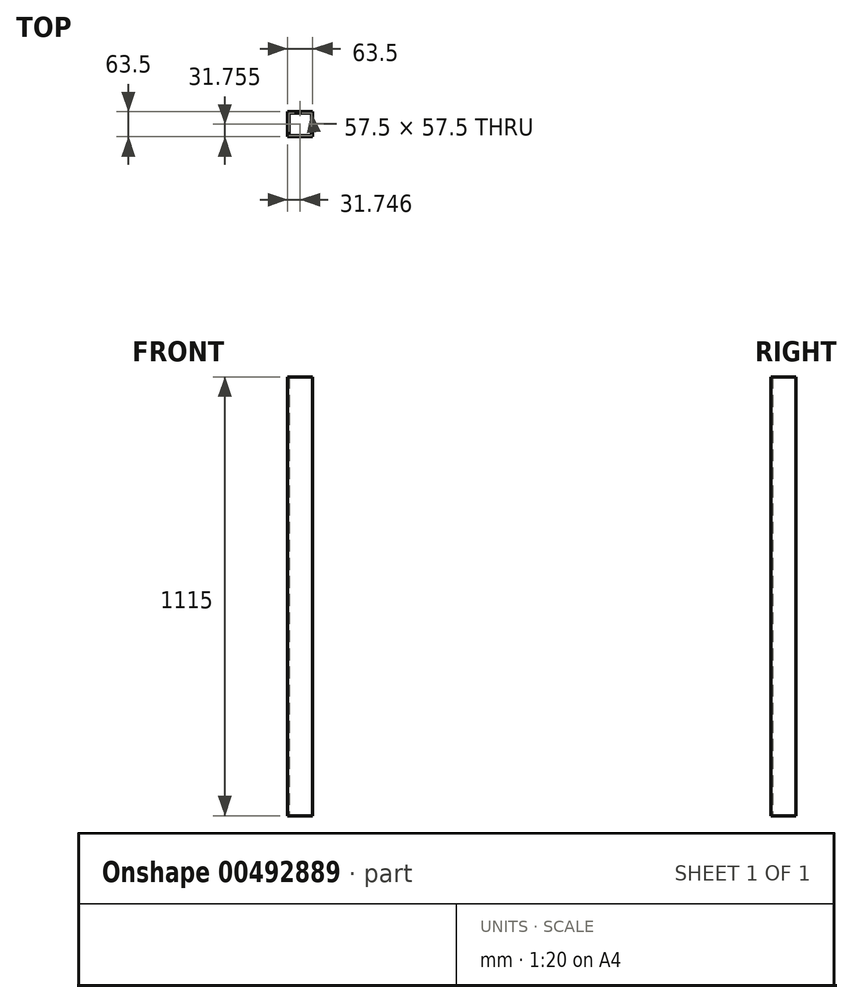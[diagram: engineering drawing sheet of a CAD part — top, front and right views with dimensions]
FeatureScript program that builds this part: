
annotation { "Feature Type Name" : "Feature", "Feature Type Description" : "" }
export const myFeature = defineFeature(function(context is Context, id is Id, definition is map)
    precondition{}
    {
        {
            var Q0;
            Q0=qCreatedBy(makeId("Top.planeOp"),FACE);
            var sketch = newSketch(context, id + "F0", { "sketchPlane" : qUnion([Q0])});
            skLineSegment(sketch, "E0.bottom", {"start": v(-23.06, 14.38) * mm, "end": v(34.44, 14.38) * mm});
            skLineSegment(sketch, "E0.top", {"start": v(-23.06, -43.12) * mm, "end": v(34.44, -43.12) * mm});
            skLineSegment(sketch, "E0.left", {"start": v(-23.06, 14.38) * mm, "end": v(-23.06, -43.12) * mm});
            skLineSegment(sketch, "E0.right", {"start": v(34.44, 14.38) * mm, "end": v(34.44, -43.12) * mm});
            skLineSegment(sketch, "E1.bottom", {"start": v(-26.06, 17.38) * mm, "end": v(37.44, 17.38) * mm});
            skLineSegment(sketch, "E1.top", {"start": v(-26.06, -46.12) * mm, "end": v(37.44, -46.12) * mm});
            skLineSegment(sketch, "E1.left", {"start": v(-26.06, 17.38) * mm, "end": v(-26.06, -46.12) * mm});
            skLineSegment(sketch, "E1.right", {"start": v(37.44, 17.38) * mm, "end": v(37.44, -46.12) * mm});
            skSolve(sketch);
        }
        {
            var Q0;
            Q0=qSketchRegion(id+"F0",true);
            extrude(context, id + "F1", {"entities" : qUnion([Q0]), "offsetDistance" : 25 * mm, "depth" : 1115 * mm});
        }
    });
